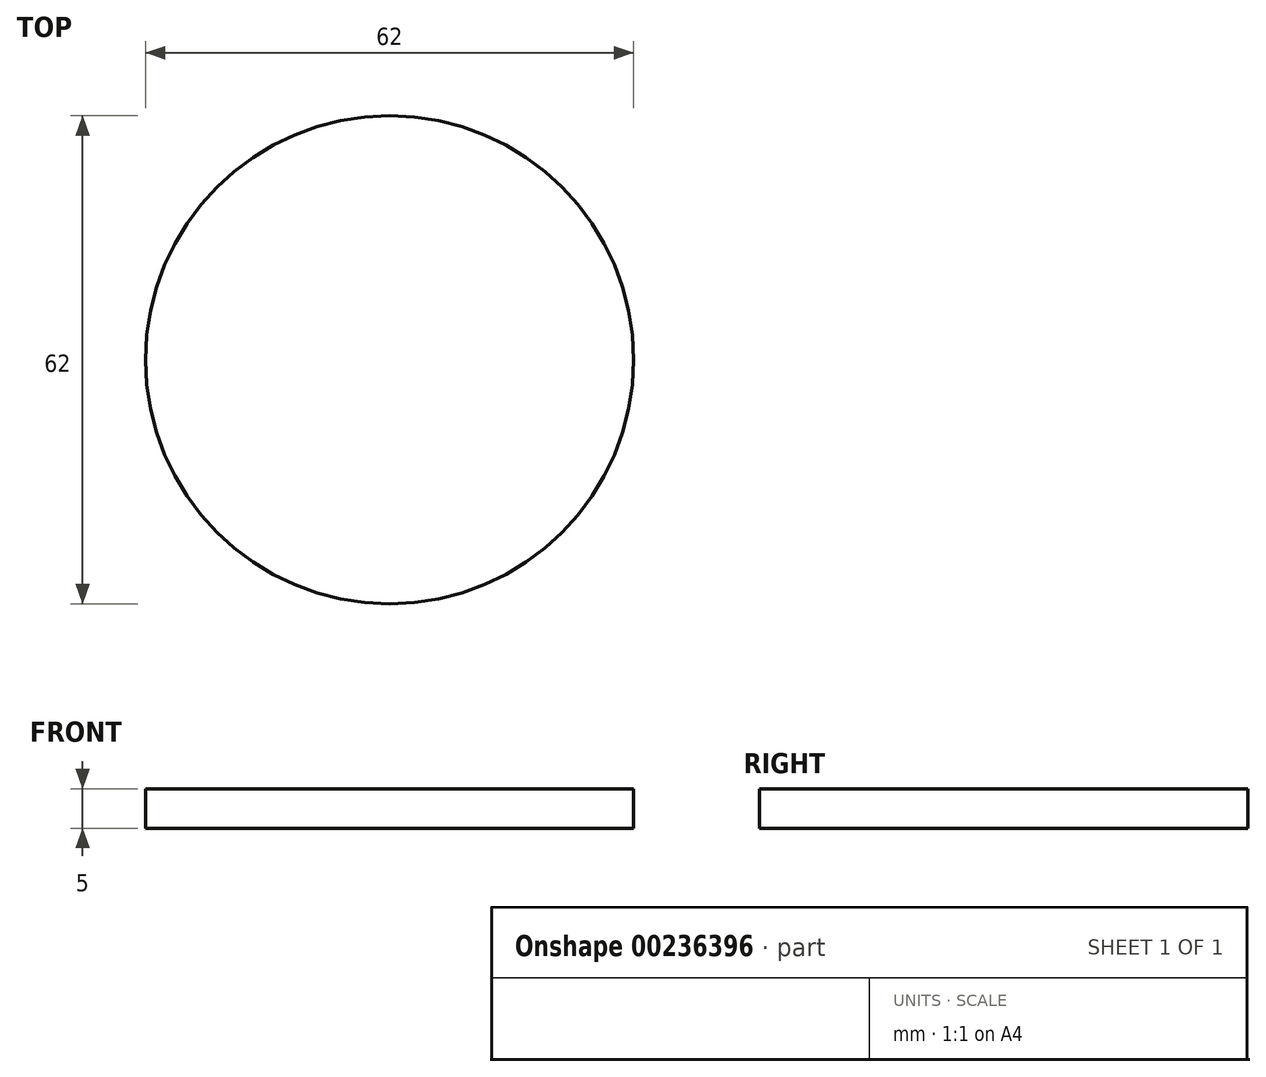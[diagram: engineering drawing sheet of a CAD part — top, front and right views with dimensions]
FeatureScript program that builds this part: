
annotation { "Feature Type Name" : "Feature", "Feature Type Description" : "" }
export const myFeature = defineFeature(function(context is Context, id is Id, definition is map)
    precondition{}
    {
        {
            var Q0;
            Q0=qCreatedBy(makeId("Top.planeOp"),FACE);
            var sketch = newSketch(context, id + "F0", { "sketchPlane" : qUnion([Q0])});
            skCircle(sketch, "E0", {"center": v(0, 0) * mm, "radius": 31 * mm});
            skSolve(sketch);
        }
        {
            var Q0;
            Q0 = qSketchRegion(id + "F0", true);
            extrude(context, id + "F1", {"entities" : qUnion([Q0]), "depth" : 5 * mm});
        }
    });
